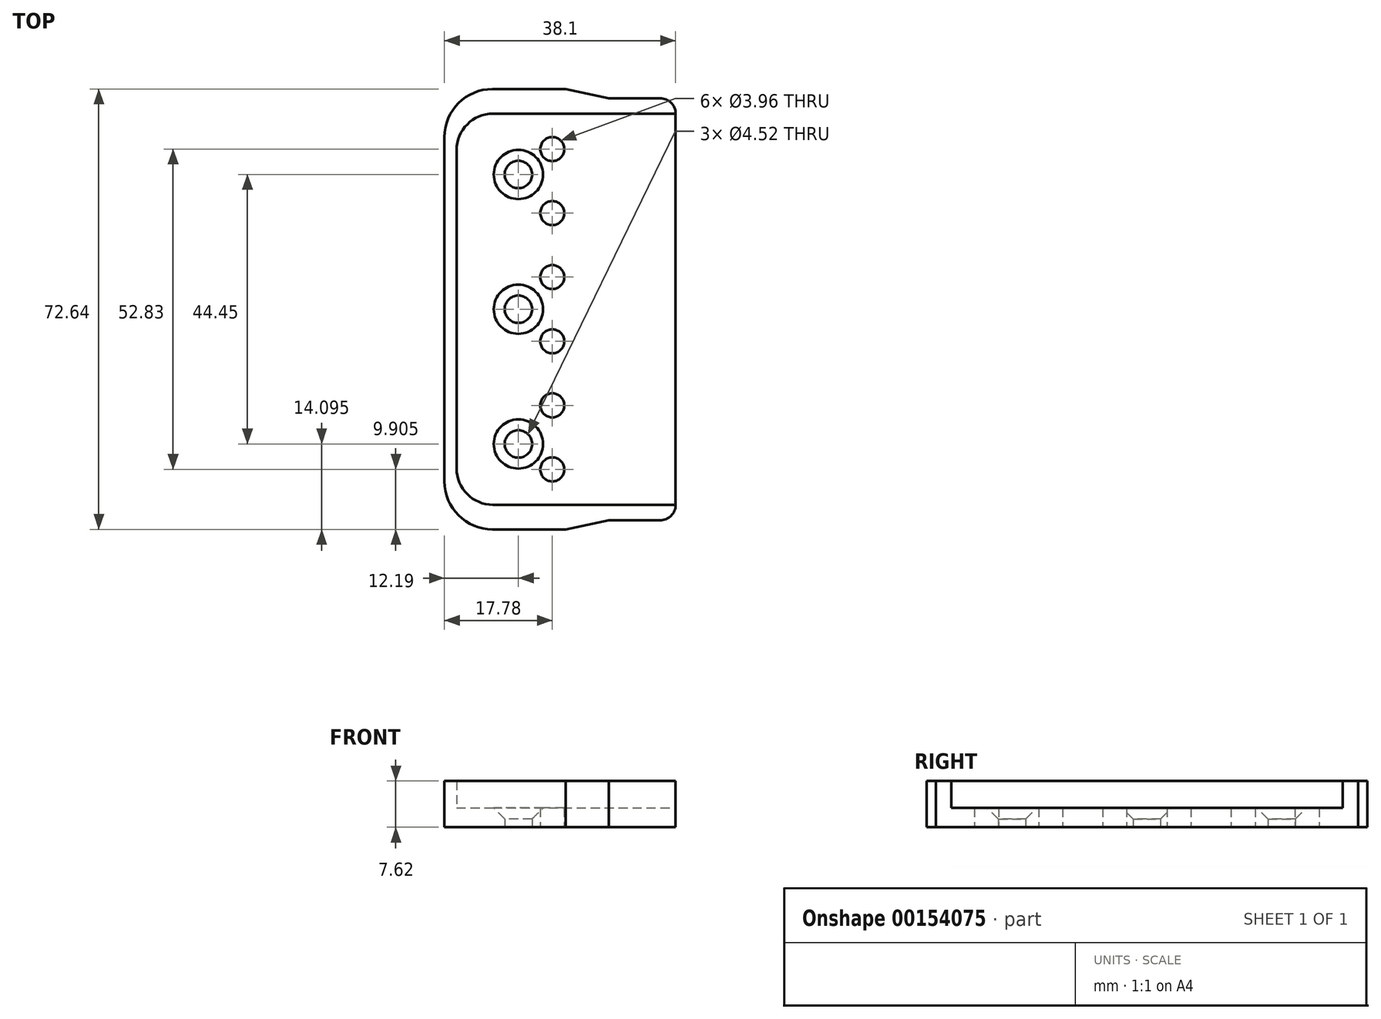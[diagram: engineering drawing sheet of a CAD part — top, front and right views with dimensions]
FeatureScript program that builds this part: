
annotation { "Feature Type Name" : "Feature", "Feature Type Description" : "" }
export const myFeature = defineFeature(function(context is Context, id is Id, definition is map)
    precondition{}
    {
        {
            var Q0;
            Q0=qCreatedBy(makeId("Top.planeOp"),FACE);
            var sketch = newSketch(context, id + "F0", { "sketchPlane" : qUnion([Q0])});
            skLineSegment(sketch, "E0", {"start": v(0, 0) * mm, "end": v(0, 32.25) * mm});
            skLineSegment(sketch, "E1", {"start": v(69.67, 0) * mm, "end": v(-138.57, 0) * mm, "construction": true});
            skLineSegment(sketch, "E2", {"start": v(-38.1, 0) * mm, "end": v(-38.1, 28.4) * mm});
            skLineSegment(sketch, "E3", {"start": v(-30.18, 36.32) * mm, "end": v(-18.1, 36.32) * mm});
            skLineSegment(sketch, "E4", {"start": v(-18.1, 36.32) * mm, "end": v(-11, 34.8) * mm});
            skLineSegment(sketch, "E5", {"start": v(-11, 34.8) * mm, "end": v(-2.54, 34.8) * mm});
            skLineSegment(sketch, "E6", {"start": v(-20.32, 48.76) * mm, "end": v(-20.32, -63.6) * mm, "construction": true});
            skCircle(sketch, "E7", {"center": v(-20.32, 26.41) * mm, "radius": 1.98 * mm});
            skCircle(sketch, "E8", {"center": v(-20.32, 15.85) * mm, "radius": 1.98 * mm});
            skCircle(sketch, "E9", {"center": v(-20.32, 5.3) * mm, "radius": 1.98 * mm});
            skCircle(sketch, "E10.MirrorC", {"center": v(-20.32, -15.85) * mm, "radius": 1.98 * mm});
            skLineSegment(sketch, "E11.MirrorCS", {"start": v(-11, -34.8) * mm, "end": v(-2.54, -34.8) * mm});
            skLineSegment(sketch, "E12.MirrorCS", {"start": v(-18.1, -36.32) * mm, "end": v(-11, -34.8) * mm});
            skLineSegment(sketch, "E13.MirrorCS", {"start": v(-38.1, 0) * mm, "end": v(-38.1, -28.4) * mm});
            skLineSegment(sketch, "E14.MirrorCS", {"start": v(-20.32, -48.76) * mm, "end": v(-20.32, 63.6) * mm, "construction": true});
            skLineSegment(sketch, "E15.MirrorCS", {"start": v(0, 0) * mm, "end": v(0, -32.26) * mm});
            skLineSegment(sketch, "E16.MirrorCS", {"start": v(-30.18, -36.32) * mm, "end": v(-18.1, -36.32) * mm});
            skCircle(sketch, "E17.MirrorC", {"center": v(-20.32, -26.41) * mm, "radius": 1.98 * mm});
            skCircle(sketch, "E18.MirrorC", {"center": v(-20.32, -5.3) * mm, "radius": 1.98 * mm});
            skPoint(sketch, "E19.visualSharp", {"position": v(-38.1, 36.32) * mm});
            skArc(sketch, "E19.filletArc", {"start": v(-30.18, 36.32) * mm, "mid": v(-35.78, 34) * mm, "end": v(-38.1, 28.4) * mm});
            skPoint(sketch, "E20.visualSharp", {"position": v(-38.1, -36.32) * mm});
            skArc(sketch, "E20.filletArc", {"start": v(-38.1, -28.4) * mm, "mid": v(-35.78, -34) * mm, "end": v(-30.18, -36.32) * mm});
            skPoint(sketch, "E21.visualSharp", {"position": v(0, 34.8) * mm});
            skArc(sketch, "E21.filletArc", {"start": v(0, 32.25) * mm, "mid": v(-0.74, 34.05) * mm, "end": v(-2.54, 34.8) * mm});
            skPoint(sketch, "E22.visualSharp", {"position": v(0, -34.8) * mm});
            skArc(sketch, "E22.filletArc", {"start": v(-2.54, -34.8) * mm, "mid": v(-0.74, -34.05) * mm, "end": v(0, -32.26) * mm});
            skLineSegment(sketch, "E23", {"start": v(-25.91, 54.64) * mm, "end": v(-25.91, -67.06) * mm, "construction": true});
            skCircle(sketch, "E24", {"center": v(-25.91, -22.23) * mm, "radius": 2.26 * mm});
            skCircle(sketch, "E25.MirrorC", {"center": v(-25.91, 22.23) * mm, "radius": 2.26 * mm});
            skCircle(sketch, "E26", {"center": v(-25.91, 0) * mm, "radius": 2.26 * mm});
            skLineSegment(sketch, "E27", {"start": v(0, -32.26) * mm, "end": v(-30.1, -32.26) * mm});
            skLineSegment(sketch, "E28", {"start": v(-36.1, -26.26) * mm, "end": v(-36.1, 26.25) * mm});
            skLineSegment(sketch, "E29", {"start": v(-30.1, 32.25) * mm, "end": v(0, 32.25) * mm});
            skPoint(sketch, "E30.visualSharp", {"position": v(-36.1, 32.25) * mm});
            skArc(sketch, "E30.filletArc", {"start": v(-30.1, 32.25) * mm, "mid": v(-34.34, 30.5) * mm, "end": v(-36.1, 26.25) * mm});
            skPoint(sketch, "E31.visualSharp", {"position": v(-36.1, -32.26) * mm});
            skArc(sketch, "E31.filletArc", {"start": v(-36.1, -26.26) * mm, "mid": v(-34.34, -30.5) * mm, "end": v(-30.1, -32.26) * mm});
            skSolve(sketch);
        }
        {
            var Q0;
            Q0=qSketchRegion(id+"F0",true);
            extrude(context, id + "F1", {"entities" : qUnion([Q0]), "depth" : 3.17 * mm});
        }
        {
            var Q0;
            Q0=makeQuery(id+"F0.imprint","IMPRINT",FACE,{"disambiguationData":[TD([[makeQuery(id+"F0.imprint","IMPRINT",EDGE,{"derivedFrom":sQuery(id+"F0.wireOp",EDGE,"E2")}),-1.0]])]});
            extrude(context, id + "F2", {"entities" : qUnion([Q0]), "operationType" : NewBodyOperationType.ADD, "depth" : (2.54 * 3) * mm});
        }
        {
            var Q0;
            Q0=makeQuery(id+"F1.opExtrude","CAP_EDGE",EDGE,{"disambiguationData":[OSD([sQuery(id+"F0.wireOp",EDGE,"E24")])],"isStart":false});
            var Q1;
            Q1=makeQuery(id+"F1.opExtrude","CAP_EDGE",EDGE,{"disambiguationData":[OSD([sQuery(id+"F0.wireOp",EDGE,"E26")])],"isStart":false});
            var Q2;
            Q2=makeQuery(id+"F1.opExtrude","CAP_EDGE",EDGE,{"disambiguationData":[OSD([sQuery(id+"F0.wireOp",EDGE,"E25.MirrorC")])],"isStart":false});
            chamfer(context, id + "F3", {"entities" : qUnion([Q0, Q1, Q2]), "width" : 1.8 * mm, "tangentPropagation" : true});
        }
        {
            var Q0;
            Q0=makeQuery(id+"F1.opExtrude","SWEPT_BODY",BODY,{"disambiguationData":[OSD([sQuery(id+"F0.wireOp",EDGE,"E0"),sQuery(id+"F0.wireOp",EDGE,"E2"),sQuery(id+"F0.wireOp",EDGE,"E3"),sQuery(id+"F0.wireOp",EDGE,"E4"),sQuery(id+"F0.wireOp",EDGE,"E5"),sQuery(id+"F0.wireOp",EDGE,"E7"),sQuery(id+"F0.wireOp",EDGE,"E8"),sQuery(id+"F0.wireOp",EDGE,"E9"),sQuery(id+"F0.wireOp",EDGE,"E10.MirrorC"),sQuery(id+"F0.wireOp",EDGE,"E11.MirrorCS"),sQuery(id+"F0.wireOp",EDGE,"E12.MirrorCS"),sQuery(id+"F0.wireOp",EDGE,"E13.MirrorCS"),sQuery(id+"F0.wireOp",EDGE,"E15.MirrorCS"),sQuery(id+"F0.wireOp",EDGE,"E16.MirrorCS"),sQuery(id+"F0.wireOp",EDGE,"E17.MirrorC"),sQuery(id+"F0.wireOp",EDGE,"E18.MirrorC"),sQuery(id+"F0.wireOp",EDGE,"E19.filletArc"),sQuery(id+"F0.wireOp",EDGE,"E20.filletArc"),sQuery(id+"F0.wireOp",EDGE,"E21.filletArc"),sQuery(id+"F0.wireOp",EDGE,"E22.filletArc"),sQuery(id+"F0.wireOp",EDGE,"E24"),sQuery(id+"F0.wireOp",EDGE,"E25.MirrorC"),sQuery(id+"F0.wireOp",EDGE,"E26")])]});
            transform(context, id + "F4", {"entities" : qUnion([Q0]), "transformType" : TransformType.TRANSLATION_3D, "dx" : 0 * mm, "dy" : 0 * mm, "dz" : 0 * mm, "makeCopy" : true});
        }
        {
            var Q0;
            Q0=makeQuery(id+"F4.opPattern","COPY",BODY,{"derivedFrom":makeQuery(id+"F1.opExtrude","SWEPT_BODY",BODY,{"disambiguationData":[OSD([sQuery(id+"F0.wireOp",EDGE,"E0"),sQuery(id+"F0.wireOp",EDGE,"E2"),sQuery(id+"F0.wireOp",EDGE,"E3"),sQuery(id+"F0.wireOp",EDGE,"E4"),sQuery(id+"F0.wireOp",EDGE,"E5"),sQuery(id+"F0.wireOp",EDGE,"E7"),sQuery(id+"F0.wireOp",EDGE,"E8"),sQuery(id+"F0.wireOp",EDGE,"E9"),sQuery(id+"F0.wireOp",EDGE,"E10.MirrorC"),sQuery(id+"F0.wireOp",EDGE,"E11.MirrorCS"),sQuery(id+"F0.wireOp",EDGE,"E12.MirrorCS"),sQuery(id+"F0.wireOp",EDGE,"E13.MirrorCS"),sQuery(id+"F0.wireOp",EDGE,"E15.MirrorCS"),sQuery(id+"F0.wireOp",EDGE,"E16.MirrorCS"),sQuery(id+"F0.wireOp",EDGE,"E17.MirrorC"),sQuery(id+"F0.wireOp",EDGE,"E18.MirrorC"),sQuery(id+"F0.wireOp",EDGE,"E19.filletArc"),sQuery(id+"F0.wireOp",EDGE,"E20.filletArc"),sQuery(id+"F0.wireOp",EDGE,"E21.filletArc"),sQuery(id+"F0.wireOp",EDGE,"E22.filletArc"),sQuery(id+"F0.wireOp",EDGE,"E24"),sQuery(id+"F0.wireOp",EDGE,"E25.MirrorC"),sQuery(id+"F0.wireOp",EDGE,"E26")])]}),"instanceName":"1"});
            deleteBodies(context, id + "F5", {"entities" : qUnion([Q0])});
        }
    });
